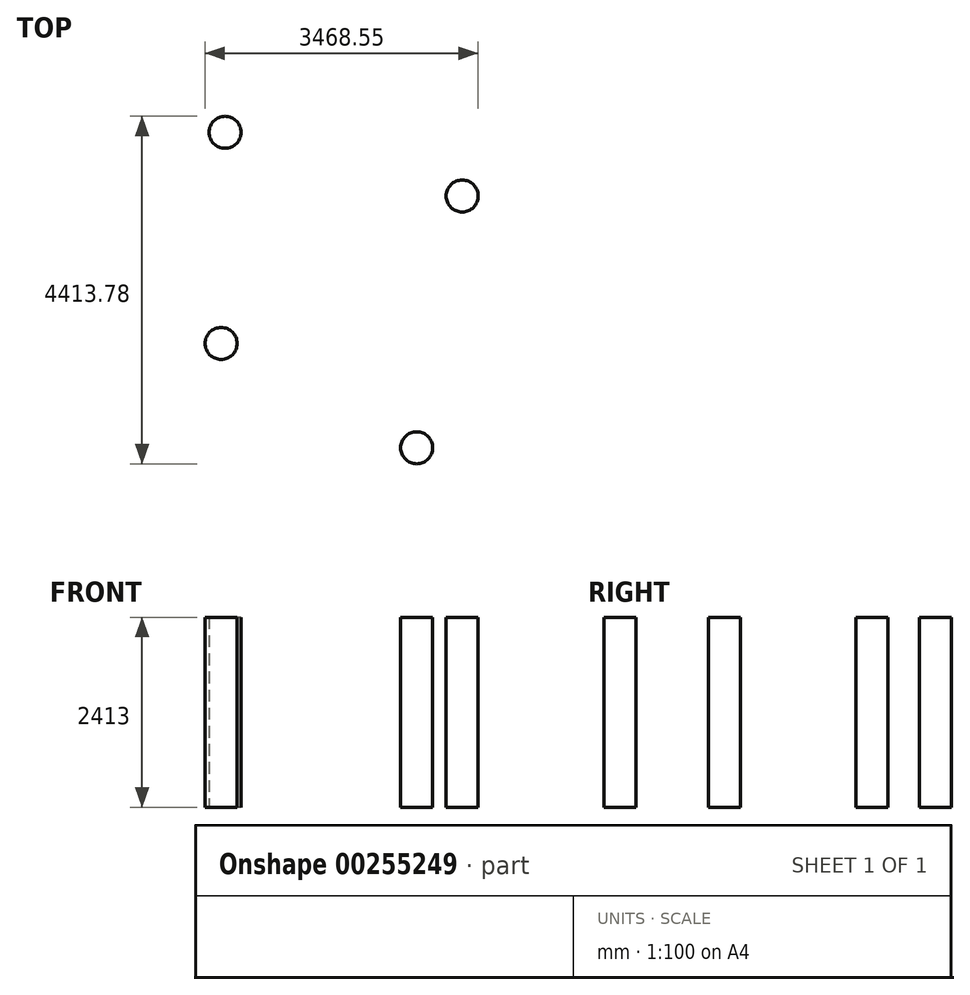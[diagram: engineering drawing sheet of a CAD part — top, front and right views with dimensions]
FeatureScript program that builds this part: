
annotation { "Feature Type Name" : "Feature", "Feature Type Description" : "" }
export const myFeature = defineFeature(function(context is Context, id is Id, definition is map)
    precondition{}
    {
        {
            var Q0;
            Q0=qCreatedBy(makeId("Top.planeOp"),FACE);
            var sketch = newSketch(context, id + "F0", { "sketchPlane" : qUnion([Q0])});
            skCircle(sketch, "E0", {"center": v(-160.79, -124.25) * mm, "radius": 203.2 * mm});
            skLineSegment(sketch, "E1", {"start": v(0, 0) * mm, "end": v(0, 2387.6) * mm});
            skCircle(sketch, "E2", {"center": v(-110.23, 2558.3) * mm, "radius": 203.2 * mm});
            skCircle(sketch, "E3", {"center": v(2901.36, 1749) * mm, "radius": 203.2 * mm});
            skCircle(sketch, "E4", {"center": v(2323.87, -1449.08) * mm, "radius": 203.2 * mm});
            skSolve(sketch);
        }
        {
            var Q0;
            Q0 = qSketchRegion(id + "F0", true);
            extrude(context, id + "F1", {"entities" : qUnion([Q0]), "depth" : 2413 * mm});
        }
    });
